# Revit family: LTGR22
name_source: partatom
category: Lighting Fixtures
revit_build: Autodesk Revit 2014 (Build: 20130308_1515(x64)
units: mm (PartAtom-declared; Revit-internal decimal feet)

## types (1)
- LTGR22
    Apparent Load = 0 VA
    Assembly Code = D5020200
    Color Filter = 16777215
    Default Elevation = 48 "
    Description = An attractive specification grade solution for indoor commercial applications, LTGR delivers high efficacy lumen packages ranging from 2,475 to 9,200, and two architecturally styled lens options
    Dimming Lamp Color Temperature Shift = <None>
    Emit Shape Visible in Rendering = No
    Emit from Rectangle Length = 22.75 "
    Emit from Rectangle Width = 22.75 "
    Fixture Distribution = Direct-Symmetric
    Glass = Paint - Hubbell - White
    Housing Material = Paint - Hubbell - White
    Lamp = LED
    Load Classification = Lighting
    Manufacturer = Hubbell Lighting
    Model = 2'X2' Recessed Linear Troffers
    Mounting = Recessed
    Photometric Link = https://www.hubbell.com
    Photometric Notes = More IES files download on Photometric Link
    Photometric Web File = LTGR22-30HLx-Rx-EDU.ies
    Power Factor = 1
    Product Documentation Link = https://hubbellcdn.com
    Product Page URL = https://www.hubbell.com
    Tilt Angle = -90.00°
    Type Comments = Lighting Fixture
    URL = https://www.hubbell.com
    Voltage = 120 V
    Warranty = 5-Years Warranty
    Width = 23.75 "
    zz Length 1 = 23.75 "

## geometry (parser evidence)
native form markers: Sweep x1
no freeform markers — native parametric forms only
